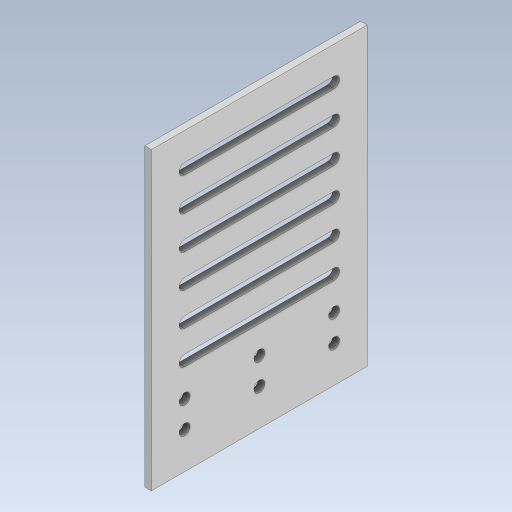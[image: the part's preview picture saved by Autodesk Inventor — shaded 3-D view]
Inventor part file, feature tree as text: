
AUTODESK INVENTOR PART (.ipt)
format: ipt  version: 2023.5 (Build 275446000, 446)  size: 166,912 bytes
history: native  units: mm
features: extrude x1, sketch x1
ambient origin geometry x8: Origin, YZ Plane, XZ Plane, XY Plane, X Axis, Y Axis, Z Axis, Center Point
bodies: Body1 (feature_tree)
feature tree (2):
  extrude  "Extrusion2"  Depth=3.3mm
  sketch  "Sketch1"  dims[d0=3.3mm d1=3.3mm d5=3.3mm d22=10.0mm d23=10.0mm d24=22.5mm d25=22.5mm d26=3.3mm d27=3.3mm d28=2.0mm d29=0.0mm d30=70.0mm d31=3.3mm d32=10.0mm d33=3.3mm d34=60.0mm d36=10.0mm d37=10.0mm d39=10.0mm]
